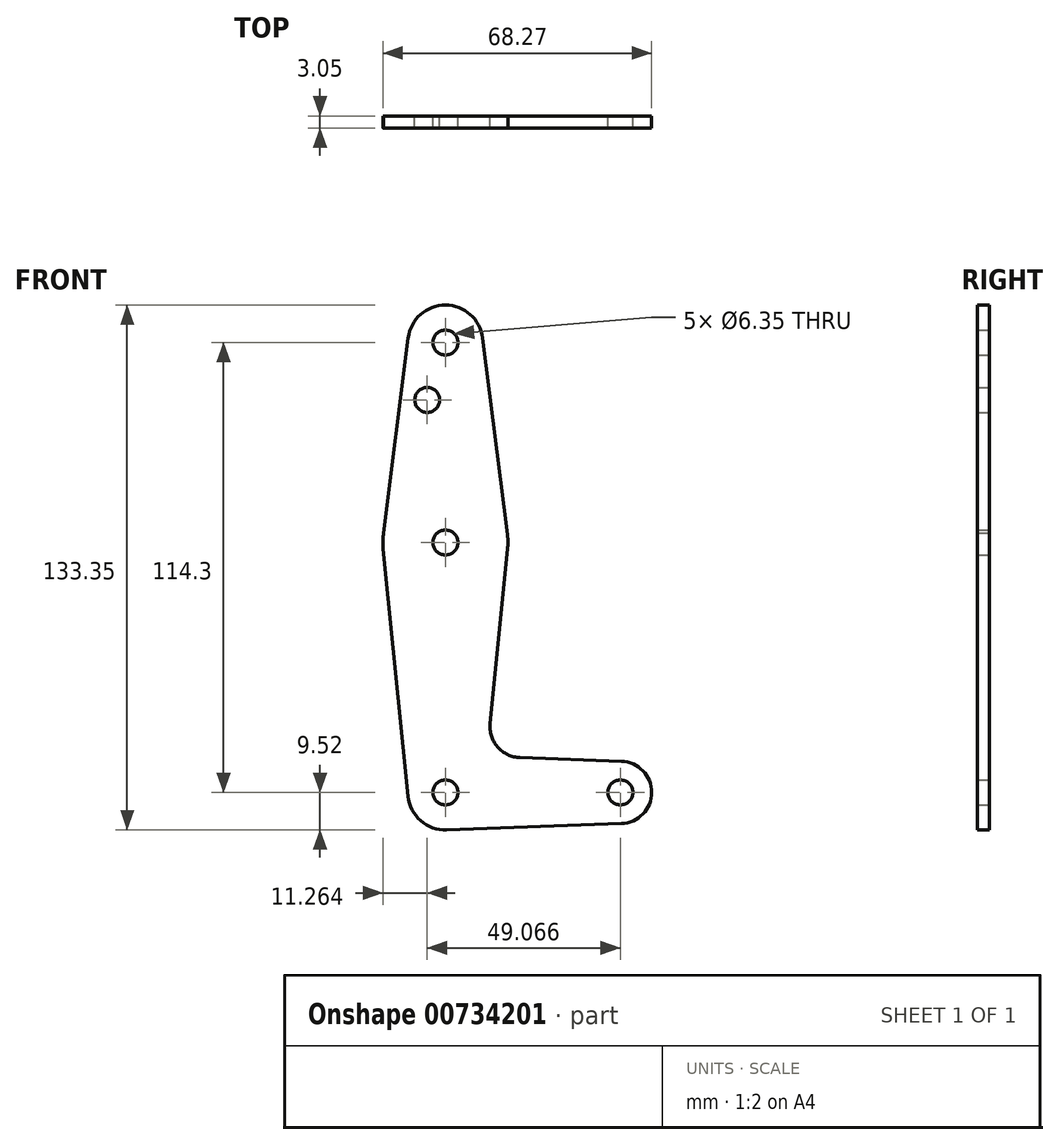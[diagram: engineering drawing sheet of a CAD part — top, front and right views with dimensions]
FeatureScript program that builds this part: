
annotation { "Feature Type Name" : "Feature", "Feature Type Description" : "" }
export const myFeature = defineFeature(function(context is Context, id is Id, definition is map)
    precondition{}
    {
        {
            var Q0;
            Q0=qCreatedBy(makeId("Front.planeOp"),FACE);
            var sketch = newSketch(context, id + "F0", { "sketchPlane" : qUnion([Q0])});
            skLineSegment(sketch, "E0", {"start": v(0, 0) * mm, "end": v(0, 114.3) * mm, "construction": true});
            skLineSegment(sketch, "E1", {"start": v(0, 0) * mm, "end": v(44.45, 0) * mm, "construction": true});
            skCircle(sketch, "E2", {"center": v(0, 114.3) * mm, "radius": 9.53 * mm});
            skCircle(sketch, "E3", {"center": v(0, 0) * mm, "radius": 9.53 * mm});
            skCircle(sketch, "E4", {"center": v(44.45, 0) * mm, "radius": 7.94 * mm});
            skCircle(sketch, "E5", {"center": v(0, 63.5) * mm, "radius": 15.88 * mm});
            skLineSegment(sketch, "E6", {"start": v(0, 63.5) * mm, "end": v(0, 0) * mm});
            skLineSegment(sketch, "E7", {"start": v(9.45, 115.5) * mm, "end": v(15.75, 65.48) * mm});
            skLineSegment(sketch, "E8", {"start": v(-9.45, 115.49) * mm, "end": v(-15.8, 65.09) * mm});
            skLineSegment(sketch, "E9", {"start": v(15.8, 61.91) * mm, "end": v(11.34, 17.59) * mm});
            skLineSegment(sketch, "E10", {"start": v(-15.8, 61.91) * mm, "end": v(-9.48, -0.95) * mm});
            skLineSegment(sketch, "E11", {"start": v(18.97, 8.85) * mm, "end": v(44.73, 7.93) * mm});
            skLineSegment(sketch, "E12", {"start": v(44.73, -7.93) * mm, "end": v(0.34, -9.52) * mm});
            skCircle(sketch, "E13", {"center": v(0, 114.3) * mm, "radius": 3.18 * mm});
            skCircle(sketch, "E14", {"center": v(0, 63.5) * mm, "radius": 3.18 * mm});
            skCircle(sketch, "E15", {"center": v(44.45, 0) * mm, "radius": 3.18 * mm});
            skCircle(sketch, "E16", {"center": v(0, 0) * mm, "radius": 3.18 * mm});
            skPoint(sketch, "E17.newPointB", {"position": v(0, 9.53) * mm});
            skArc(sketch, "E17.filletArc", {"start": v(11.34, 17.59) * mm, "mid": v(13.26, 11.57) * mm, "end": v(18.97, 8.85) * mm});
            skCircle(sketch, "E18", {"center": v(-4.62, 99.73) * mm, "radius": 3.18 * mm});
            skSolve(sketch);
        }
        {
            var Q0;
            Q0 = qSketchRegion(id + "F0", true);
            extrude(context, id + "F1", {"entities" : qUnion([Q0]), "depth" : 3.05 * mm, "offsetDistance" : 25.4 * mm});
        }
    });
